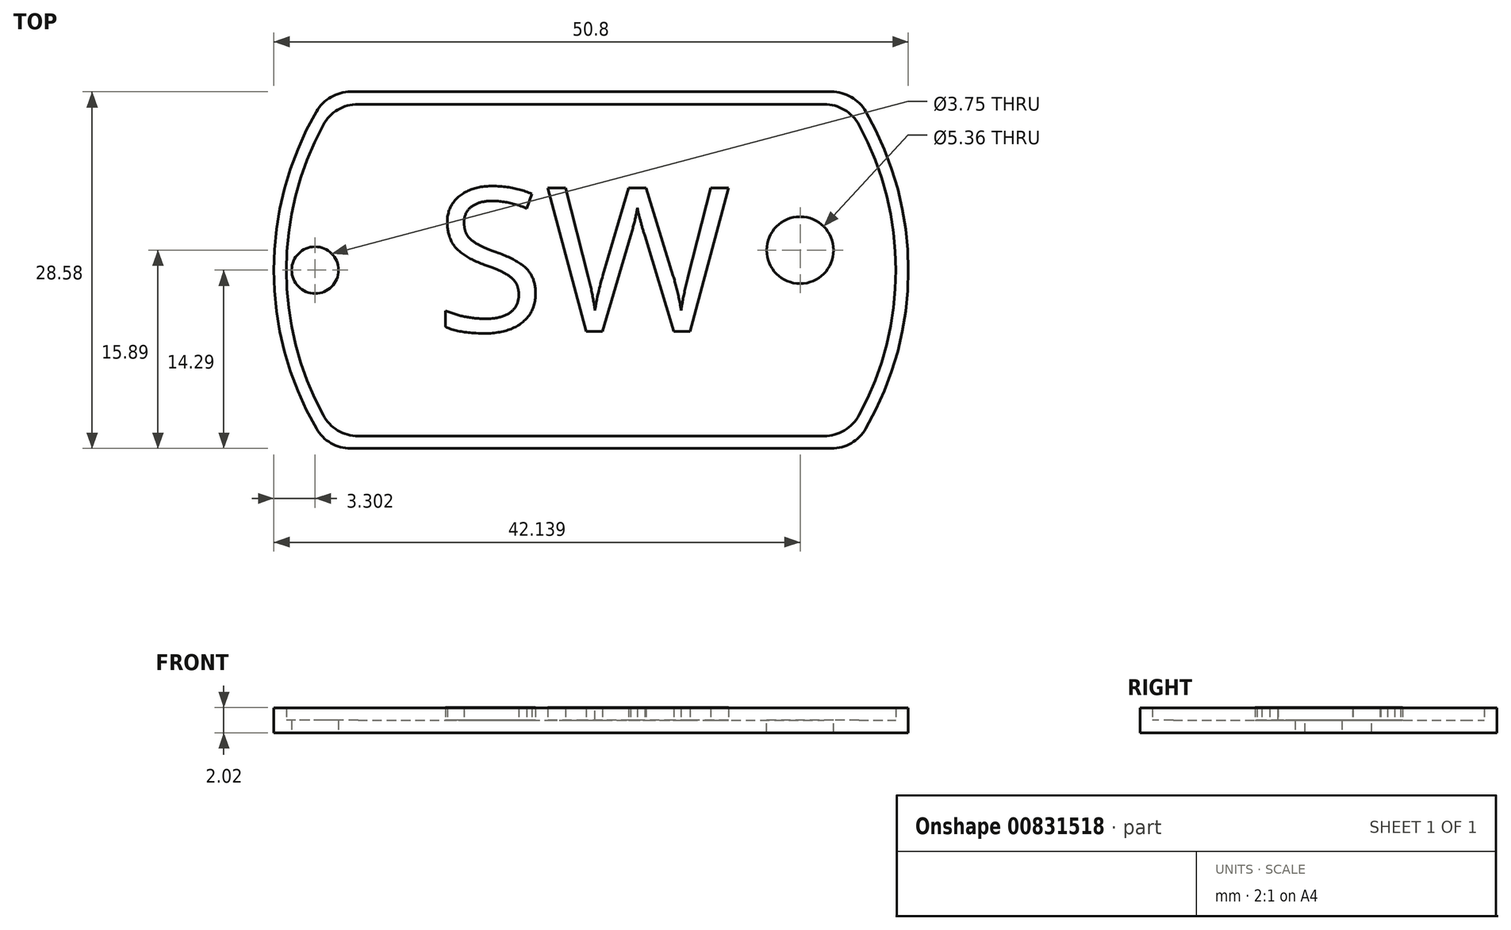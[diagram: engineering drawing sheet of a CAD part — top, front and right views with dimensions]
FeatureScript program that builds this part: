
annotation { "Feature Type Name" : "Feature", "Feature Type Description" : "" }
export const myFeature = defineFeature(function(context is Context, id is Id, definition is map)
    precondition{}
    {
        {
            var Q0;
            Q0=qCreatedBy(makeId("Top.planeOp"),FACE);
            var sketch = newSketch(context, id + "F0", { "sketchPlane" : qUnion([Q0])});
            skArc(sketch, "E0", {"start": v(-22, 12.7) * mm, "mid": v(-25.4, 0) * mm, "end": v(-22, -12.7) * mm});
            skLineSegment(sketch, "E1.top", {"start": v(-19.25, -14.29) * mm, "end": v(19.25, -14.29) * mm});
            skArc(sketch, "E2.trimOffspring", {"start": v(22, -12.7) * mm, "mid": v(25.4, 0) * mm, "end": v(22, 12.7) * mm});
            skLineSegment(sketch, "E3", {"start": v(-19.25, 14.29) * mm, "end": v(19.25, 14.29) * mm});
            skPoint(sketch, "E4.visualSharp", {"position": v(-21, 14.29) * mm});
            skArc(sketch, "E4.filletArc", {"start": v(-19.25, 14.29) * mm, "mid": v(-20.83, 13.86) * mm, "end": v(-22, 12.7) * mm});
            skPoint(sketch, "E5.visualSharp", {"position": v(21, 14.29) * mm});
            skArc(sketch, "E5.filletArc", {"start": v(22, 12.7) * mm, "mid": v(20.83, 13.86) * mm, "end": v(19.25, 14.29) * mm});
            skPoint(sketch, "E6.visualSharp", {"position": v(21, -14.29) * mm});
            skArc(sketch, "E6.filletArc", {"start": v(19.25, -14.29) * mm, "mid": v(20.83, -13.86) * mm, "end": v(22, -12.7) * mm});
            skPoint(sketch, "E7.visualSharp", {"position": v(-21, -14.29) * mm});
            skArc(sketch, "E7.filletArc", {"start": v(-22, -12.7) * mm, "mid": v(-20.83, -13.86) * mm, "end": v(-19.25, -14.29) * mm});
            skCircle(sketch, "E8", {"center": v(-22.1, 0) * mm, "radius": 1.87 * mm});
            skSolve(sketch);
        }
        {
            var Q0;
            Q0=makeQuery(id+"F0.imprint","IMPRINT",FACE,{"disambiguationData":[TD([[makeQuery(id+"F0.imprint","IMPRINT",EDGE,{"derivedFrom":sQuery(id+"F0.wireOp",EDGE,"E0")}),1.0]])]});
            extrude(context, id + "F1", {"entities" : qUnion([Q0]), "depth" : 1 * mm, "offsetDistance" : 25.4 * mm});
        }
        {
            var Q0;
            Q0=makeQuery(id+"F1.opExtrude","CAP_FACE",FACE,{"disambiguationData":[OSD([sQuery(id+"F0.wireOp",EDGE,"E0"),sQuery(id+"F0.wireOp",EDGE,"E1.top"),sQuery(id+"F0.wireOp",EDGE,"E2.trimOffspring"),sQuery(id+"F0.wireOp",EDGE,"E3"),sQuery(id+"F0.wireOp",EDGE,"E4.filletArc"),sQuery(id+"F0.wireOp",EDGE,"E5.filletArc"),sQuery(id+"F0.wireOp",EDGE,"E6.filletArc"),sQuery(id+"F0.wireOp",EDGE,"E7.filletArc")])],"isStart":false});
            var sketch = newSketch(context, id + "F2", { "sketchPlane" : qUnion([Q0])});
            skLineSegment(sketch, "E9.0", {"start": v(-18.66, 13.29) * mm, "end": v(18.66, 13.29) * mm});
            skArc(sketch, "E9.1", {"start": v(-21.45, 11.63) * mm, "mid": v(-24.4, 0) * mm, "end": v(-21.45, -11.63) * mm});
            skLineSegment(sketch, "E9.2", {"start": v(-18.66, -13.29) * mm, "end": v(18.66, -13.29) * mm});
            skArc(sketch, "E9.3", {"start": v(21.45, -11.63) * mm, "mid": v(24.4, 0) * mm, "end": v(21.45, 11.63) * mm});
            skPoint(sketch, "E10.visualSharp", {"position": v(-20.46, 13.29) * mm});
            skArc(sketch, "E10.filletArc", {"start": v(-18.66, 13.29) * mm, "mid": v(-20.29, 12.84) * mm, "end": v(-21.45, 11.63) * mm});
            skPoint(sketch, "E11.visualSharp", {"position": v(20.46, 13.29) * mm});
            skArc(sketch, "E11.filletArc", {"start": v(21.45, 11.63) * mm, "mid": v(20.29, 12.84) * mm, "end": v(18.66, 13.29) * mm});
            skPoint(sketch, "E12.visualSharp", {"position": v(20.46, -13.29) * mm});
            skArc(sketch, "E12.filletArc", {"start": v(18.66, -13.29) * mm, "mid": v(20.29, -12.84) * mm, "end": v(21.45, -11.63) * mm});
            skPoint(sketch, "E13.visualSharp", {"position": v(-20.46, -13.29) * mm});
            skArc(sketch, "E13.filletArc", {"start": v(-21.45, -11.63) * mm, "mid": v(-20.29, -12.84) * mm, "end": v(-18.66, -13.29) * mm});
            skLineSegment(sketch, "E14.0", {"start": v(-19.25, 14.29) * mm, "end": v(19.25, 14.29) * mm});
            skArc(sketch, "E14.1", {"start": v(-22, 12.7) * mm, "mid": v(-25.4, 0) * mm, "end": v(-22, -12.7) * mm});
            skLineSegment(sketch, "E14.2", {"start": v(-19.25, -14.29) * mm, "end": v(19.25, -14.29) * mm});
            skArc(sketch, "E14.3", {"start": v(22, -12.7) * mm, "mid": v(25.4, 0) * mm, "end": v(22, 12.7) * mm});
            skPoint(sketch, "E15.visualSharp", {"position": v(-21, -14.29) * mm});
            skArc(sketch, "E15.filletArc", {"start": v(-22, -12.7) * mm, "mid": v(-20.83, -13.86) * mm, "end": v(-19.25, -14.29) * mm});
            skPoint(sketch, "E16.visualSharp", {"position": v(21, -14.29) * mm});
            skArc(sketch, "E16.filletArc", {"start": v(19.25, -14.29) * mm, "mid": v(20.83, -13.86) * mm, "end": v(22, -12.7) * mm});
            skPoint(sketch, "E17.visualSharp", {"position": v(21, 14.29) * mm});
            skArc(sketch, "E17.filletArc", {"start": v(22, 12.7) * mm, "mid": v(20.83, 13.86) * mm, "end": v(19.25, 14.29) * mm});
            skPoint(sketch, "E18.visualSharp", {"position": v(-21, 14.29) * mm});
            skArc(sketch, "E18.filletArc", {"start": v(-19.25, 14.29) * mm, "mid": v(-20.83, 13.86) * mm, "end": v(-22, 12.7) * mm});
            skSolve(sketch);
        }
        {
            var Q0;
            Q0=makeQuery(id+"F2.imprint","IMPRINT",FACE,{"disambiguationData":[TD([[makeQuery(id+"F2.imprint","IMPRINT",EDGE,{"derivedFrom":sQuery(id+"F2.wireOp",EDGE,"E9.0")}),1.0]])]});
            extrude(context, id + "F3", {"entities" : qUnion([Q0]), "operationType" : NewBodyOperationType.ADD, "depth" : 1 * mm, "offsetDistance" : 25.4 * mm});
        }
        {
            var Q0;
            Q0=makeQuery(id+"F1.opExtrude","CAP_FACE",FACE,{"disambiguationData":[OSD([sQuery(id+"F0.wireOp",EDGE,"E0"),sQuery(id+"F0.wireOp",EDGE,"E1.top"),sQuery(id+"F0.wireOp",EDGE,"E2.trimOffspring"),sQuery(id+"F0.wireOp",EDGE,"E3"),sQuery(id+"F0.wireOp",EDGE,"E4.filletArc"),sQuery(id+"F0.wireOp",EDGE,"E5.filletArc"),sQuery(id+"F0.wireOp",EDGE,"E6.filletArc"),sQuery(id+"F0.wireOp",EDGE,"E7.filletArc"),sQuery(id+"F0.wireOp",EDGE,"E8")])],"isStart":false});
            var sketch = newSketch(context, id + "F4", { "sketchPlane" : qUnion([Q0])});
            skText(sketch, "E19", { "text": "SW", "fontName": "OpenSans-Regular.ttf"});
            const initialGuessF4  = {"E19": [-0.0125, -0.00491, 1, 0, 0.01158]};
            skSetInitialGuess(sketch, initialGuessF4);
            skSolve(sketch);
        }
        {
            var Q0;
            Q0 = qSketchRegion(id + "F4", true);
            extrude(context, id + "F5", {"entities" : qUnion([Q0]), "operationType" : NewBodyOperationType.ADD, "depth" : 1.02 * mm, "offsetDistance" : 25.4 * mm});
        }
        {
            var Q0;
            Q0=makeQuery(id+"F1.opExtrude","CAP_FACE",FACE,{"disambiguationData":[OSD([sQuery(id+"F0.wireOp",EDGE,"E0"),sQuery(id+"F0.wireOp",EDGE,"E1.top"),sQuery(id+"F0.wireOp",EDGE,"E2.trimOffspring"),sQuery(id+"F0.wireOp",EDGE,"E3"),sQuery(id+"F0.wireOp",EDGE,"E4.filletArc"),sQuery(id+"F0.wireOp",EDGE,"E5.filletArc"),sQuery(id+"F0.wireOp",EDGE,"E6.filletArc"),sQuery(id+"F0.wireOp",EDGE,"E7.filletArc"),sQuery(id+"F0.wireOp",EDGE,"E8")])],"isStart":false});
            var sketch = newSketch(context, id + "F6", { "sketchPlane" : qUnion([Q0])});
            skCircle(sketch, "E20", {"center": v(16.74, 1.6) * mm, "radius": 2.68 * mm});
            skText(sketch, "E21", { "text": "Some smaller text", "fontName": "OpenSans-Regular.ttf"});
            const initialGuessF6  = {"E21": [-0.01312, -0.01051, 1, 0, 0.00286]};
            skSetInitialGuess(sketch, initialGuessF6);
            skSolve(sketch);
        }
        {
            var Q0;
            Q0=makeQuery(id+"F6.imprint","IMPRINT",FACE,{"disambiguationData":[TD([[makeQuery(id+"F6.imprint","IMPRINT",EDGE,{"derivedFrom":sQuery(id+"F6.wireOp",EDGE,"E20")}),1.0]])]});
            extrude(context, id + "F7", {"entities" : qUnion([Q0]), "operationType" : NewBodyOperationType.REMOVE, "oppositeDirection" : true, "depth" : 2.54 * mm, "offsetDistance" : 25.4 * mm});
        }
    });
